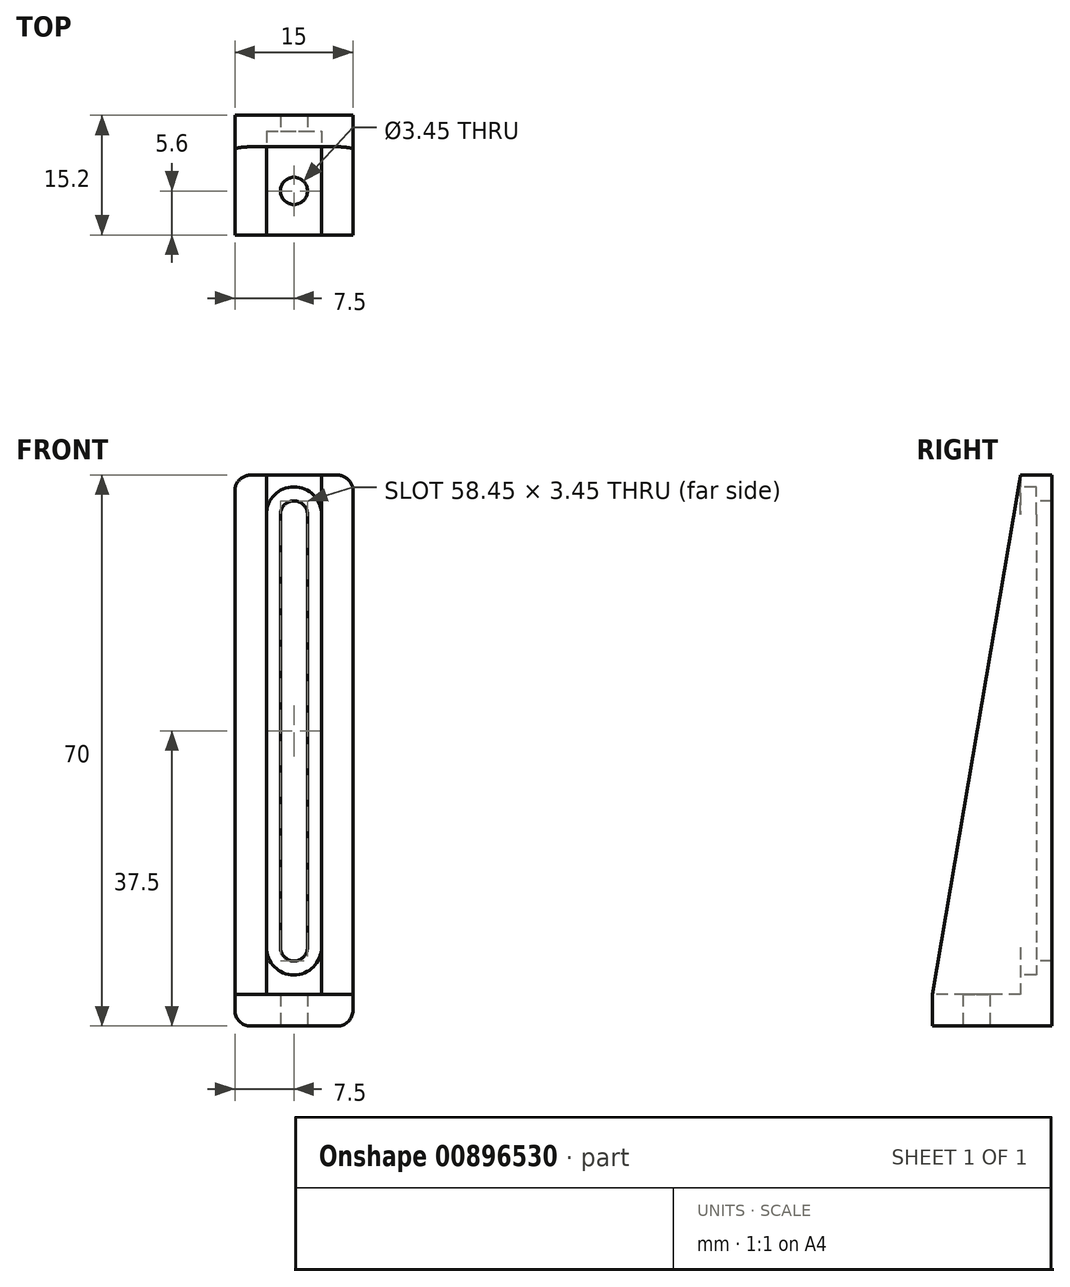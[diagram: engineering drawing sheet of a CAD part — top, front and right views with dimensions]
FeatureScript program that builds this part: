
annotation { "Feature Type Name" : "Feature", "Feature Type Description" : "" }
export const myFeature = defineFeature(function(context is Context, id is Id, definition is map)
    precondition{}
    {
        {
            var Q0;
            Q0=qCreatedBy(makeId("Top.planeOp"),FACE);
            var sketch = newSketch(context, id + "F0", { "sketchPlane" : qUnion([Q0])});
            skLineSegment(sketch, "E0.bottom", {"start": v(7.5, 7.6) * mm, "end": v(-7.5, 7.6) * mm});
            skLineSegment(sketch, "E0.top", {"start": v(7.5, -7.6) * mm, "end": v(-7.5, -7.6) * mm});
            skLineSegment(sketch, "E0.left", {"start": v(7.5, 7.6) * mm, "end": v(7.5, -7.6) * mm});
            skLineSegment(sketch, "E0.right", {"start": v(-7.5, 7.6) * mm, "end": v(-7.5, -7.6) * mm});
            skPoint(sketch, "E0.middle", {"position": v(0, 0) * mm});
            skCircle(sketch, "E1", {"center": v(0, -2) * mm, "radius": 1.73 * mm});
            skLineSegment(sketch, "E2", {"start": v(0, -2) * mm, "end": v(0, -7.6) * mm, "construction": true});
            skSolve(sketch);
        }
        {
            var Q0;
            Q0=qSketchRegion(id+"F0",true);
            extrude(context, id + "F1", {"entities" : qUnion([Q0]), "depth" : 4 * mm, "offsetDistance" : 25 * mm});
        }
        {
            var Q0;
            Q0=makeQuery(id+"F1.opExtrude","CAP_FACE",FACE,{"disambiguationData":[OSD([sQuery(id+"F0.wireOp",EDGE,"E0.bottom"),sQuery(id+"F0.wireOp",EDGE,"E0.top"),sQuery(id+"F0.wireOp",EDGE,"E0.left"),sQuery(id+"F0.wireOp",EDGE,"E0.right"),sQuery(id+"F0.wireOp",EDGE,"E1")])],"isStart":false});
            var sketch = newSketch(context, id + "F2", { "sketchPlane" : qUnion([Q0])});
            skLineSegment(sketch, "E3", {"start": v(-7.5, -7.6) * mm, "end": v(-3.5, -7.6) * mm});
            skLineSegment(sketch, "E4", {"start": v(-3.5, -7.6) * mm, "end": v(-3.5, 3.6) * mm});
            skLineSegment(sketch, "E5", {"start": v(-3.5, 3.6) * mm, "end": v(3.5, 3.6) * mm});
            skLineSegment(sketch, "E6", {"start": v(3.5, 3.6) * mm, "end": v(3.5, -7.6) * mm});
            skLineSegment(sketch, "E7", {"start": v(3.5, -7.6) * mm, "end": v(7.5, -7.6) * mm});
            skLineSegment(sketch, "E8", {"start": v(7.5, -7.6) * mm, "end": v(7.5, 7.6) * mm});
            skLineSegment(sketch, "E9", {"start": v(7.5, 7.6) * mm, "end": v(-7.5, 7.6) * mm});
            skLineSegment(sketch, "E10", {"start": v(-7.5, 7.6) * mm, "end": v(-7.5, -7.6) * mm});
            skCircle(sketch, "E11", {"center": v(0, -2) * mm, "radius": 3.5 * mm});
            skSolve(sketch);
        }
        {
            var Q0;
            {var subQ4=sQuery(id+"F2.wireOp",EDGE,"E3");Q0=makeQuery(id+"F2.imprint","IMPRINT",FACE,{"disambiguationData":[TD([[makeQuery(id+"F2.imprint","IMPRINT",EDGE,{"derivedFrom":subQ4}),-1.0]])]});}
            extrude(context, id + "F3", {"entities" : qUnion([Q0]), "operationType" : NewBodyOperationType.ADD, "depth" : 66 * mm, "offsetDistance" : 25 * mm});
        }
        {
            var Q0;
            Q0=makeQuery(id+"F3.opExtrude","SWEPT_FACE",FACE,{"disambiguationData":[OSD([sQuery(id+"F2.wireOp",EDGE,"E5")])]});
            var sketch = newSketch(context, id + "F4", { "sketchPlane" : qUnion([Q0])});
            skLineSegment(sketch, "E12", {"start": v(0, 0) * mm, "end": v(0, 65) * mm, "construction": true});
            skCircle(sketch, "E13", {"center": v(0, 65) * mm, "radius": 1.73 * mm});
            skCircle(sketch, "E14", {"center": v(0, 65) * mm, "radius": 3.5 * mm});
            skCircle(sketch, "E15", {"center": v(0, 10) * mm, "radius": 1.73 * mm});
            skCircle(sketch, "E16", {"center": v(0, 10) * mm, "radius": 3.5 * mm});
            skLineSegment(sketch, "E17", {"start": v(-1.73, 10) * mm, "end": v(-1.73, 65) * mm});
            skLineSegment(sketch, "E18", {"start": v(1.73, 65) * mm, "end": v(1.73, 10) * mm});
            skSolve(sketch);
        }
        {
            var Q0;
            {var subQ0=sQuery(id+"F4.wireOp",EDGE,"E17");var subQ1=sQuery(id+"F4.wireOp",EDGE,"E14");var subQ2=makeQuery(id+"F4.imprint","INTERSECT",VERTEX,{"derivedFrom":[subQ1,subQ0]});Q0=makeQuery(id+"F4.imprint","IMPRINT",FACE,{"disambiguationData":[TD([[makeQuery(id+"F4.imprint","IMPRINT",EDGE,{"disambiguationData":[TD([[subQ2,1.0]])],"derivedFrom":subQ0}),1.0]])]});}
            var Q1;
            {var subQ0=sQuery(id+"F4.wireOp",EDGE,"E18");var subQ1=sQuery(id+"F4.wireOp",EDGE,"E14");var subQ2=makeQuery(id+"F4.imprint","INTERSECT",VERTEX,{"derivedFrom":[subQ1,subQ0]});Q1=makeQuery(id+"F4.imprint","IMPRINT",FACE,{"disambiguationData":[TD([[makeQuery(id+"F4.imprint","IMPRINT",EDGE,{"disambiguationData":[TD([[subQ2,-1.0]])],"derivedFrom":subQ0}),1.0]])]});}
            var Q2;
            {var subQ0=sQuery(id+"F4.wireOp",EDGE,"E17");var subQ5=sQuery(id+"F4.wireOp",EDGE,"E13");var subQ6=makeQuery(id+"F4.imprint","INTERSECT",VERTEX,{"derivedFrom":[subQ5,subQ0]});Q2=makeQuery(id+"F4.imprint","IMPRINT",FACE,{"disambiguationData":[TD([[makeQuery(id+"F4.imprint","IMPRINT",EDGE,{"disambiguationData":[TD([[subQ6,1.0]])],"derivedFrom":subQ5}),-1.0]])]});}
            var Q3;
            {var subQ4=sQuery(id+"F4.wireOp",EDGE,"E17");var subQ8=sQuery(id+"F4.wireOp",EDGE,"E15");var subQ9=makeQuery(id+"F4.imprint","INTERSECT",VERTEX,{"derivedFrom":[subQ8,subQ4]});Q3=makeQuery(id+"F4.imprint","IMPRINT",FACE,{"disambiguationData":[TD([[makeQuery(id+"F4.imprint","IMPRINT",EDGE,{"disambiguationData":[TD([[subQ9,-1.0]])],"derivedFrom":subQ8}),-1.0]])]});}
            extrude(context, id + "F5", {"entities" : qUnion([Q0, Q1, Q2, Q3]), "operationType" : NewBodyOperationType.REMOVE, "oppositeDirection" : true, "depth" : 2 * mm, "offsetDistance" : 25 * mm});
        }
        {
            var Q0;
            Q0=makeQuery(id+"F4.imprint","IMPRINT",FACE,{"disambiguationData":[TD([[makeQuery(id+"F4.imprint","IMPRINT",EDGE,{"derivedFrom":sQuery(id+"F4.wireOp",EDGE,"E13")}),1.0]])]});
            var Q1;
            {var subQ0=sQuery(id+"F4.wireOp",EDGE,"E17");var subQ1=sQuery(id+"F4.wireOp",EDGE,"E13");var subQ2=makeQuery(id+"F4.imprint","INTERSECT",VERTEX,{"derivedFrom":[subQ1,subQ0]});Q1=makeQuery(id+"F4.imprint","IMPRINT",FACE,{"disambiguationData":[TD([[makeQuery(id+"F4.imprint","IMPRINT",EDGE,{"disambiguationData":[TD([[subQ2,-1.0]])],"derivedFrom":subQ1}),-1.0]])]});}
            var Q2;
            {var subQ0=sQuery(id+"F4.wireOp",EDGE,"E17");var subQ1=sQuery(id+"F4.wireOp",EDGE,"E14");var subQ2=makeQuery(id+"F4.imprint","INTERSECT",VERTEX,{"derivedFrom":[subQ1,subQ0]});Q2=makeQuery(id+"F4.imprint","IMPRINT",FACE,{"disambiguationData":[TD([[makeQuery(id+"F4.imprint","IMPRINT",EDGE,{"disambiguationData":[TD([[subQ2,-1.0]])],"derivedFrom":subQ1}),-1.0]])]});}
            var Q3;
            {var subQ0=sQuery(id+"F4.wireOp",EDGE,"E17");var subQ1=sQuery(id+"F4.wireOp",EDGE,"E15");var subQ2=makeQuery(id+"F4.imprint","INTERSECT",VERTEX,{"derivedFrom":[subQ1,subQ0]});Q3=makeQuery(id+"F4.imprint","IMPRINT",FACE,{"disambiguationData":[TD([[makeQuery(id+"F4.imprint","IMPRINT",EDGE,{"disambiguationData":[TD([[subQ2,1.0]])],"derivedFrom":subQ1}),-1.0]])]});}
            var Q4;
            {var subQ0=sQuery(id+"F4.wireOp",EDGE,"E15");var subQ1=makeQuery(id+"F4.imprint","INTERSECT",VERTEX,{"derivedFrom":[subQ0,sQuery(id+"F4.wireOp",EDGE,"E17")]});Q4=makeQuery(id+"F4.imprint","IMPRINT",FACE,{"disambiguationData":[TD([[makeQuery(id+"F4.imprint","IMPRINT",EDGE,{"disambiguationData":[TD([[subQ1,1.0]])],"derivedFrom":subQ0}),1.0]])]});}
            extrude(context, id + "F6", {"entities" : qUnion([Q0, Q1, Q2, Q3, Q4]), "operationType" : NewBodyOperationType.REMOVE, "endBound" : BoundingType.UP_TO_NEXT, "oppositeDirection" : true, "depth" : 25 * mm, "offsetDistance" : 25 * mm});
        }
        {
            var Q0;
            Q0=makeQuery(id+"F3.opExtrude","CAP_EDGE",EDGE,{"disambiguationData":[OSD([sQuery(id+"F2.wireOp",EDGE,"E7")])],"isStart":false});
            var Q1;
            Q1=makeQuery(id+"F3.opExtrude","CAP_EDGE",EDGE,{"disambiguationData":[OSD([sQuery(id+"F2.wireOp",EDGE,"E3")])],"isStart":false});
            chamfer(context, id + "F7", {"entities" : qUnion([Q0, Q1]), "chamferType" : ChamferType.TWO_OFFSETS, "width1" : 66 * mm, "oppositeDirection" : false, "width2" : 11.2 * mm, "tangentPropagation" : true});
        }
        {
            var Q0;
            Q0=makeQuery(id+"F3.opExtrude","CAP_EDGE",EDGE,{"disambiguationData":[OSD([sQuery(id+"F2.wireOp",EDGE,"E10")])],"isStart":false});
            var Q1;
            Q1=makeQuery(id+"F3.opExtrude","CAP_EDGE",EDGE,{"disambiguationData":[OSD([sQuery(id+"F2.wireOp",EDGE,"E8")])],"isStart":false});
            var Q2;
            Q2=makeQuery(id+"F1.opExtrude","CAP_EDGE",EDGE,{"disambiguationData":[OSD([sQuery(id+"F0.wireOp",EDGE,"E0.right")])],"isStart":true});
            var Q3;
            Q3=makeQuery(id+"F1.opExtrude","CAP_EDGE",EDGE,{"disambiguationData":[OSD([sQuery(id+"F0.wireOp",EDGE,"E0.left")])],"isStart":true});
            fillet(context, id + "F8", {"entities" : qUnion([Q0, Q1, Q2, Q3]), "tangentPropagation" : true, "radius" : 2 * mm, "defaultsChanged" : true, "vertexSettings" : [], "allowEdgeOverflow" : false});
        }
    });
